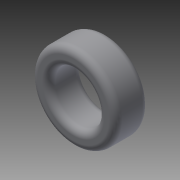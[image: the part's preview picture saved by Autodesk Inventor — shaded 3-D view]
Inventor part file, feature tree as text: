
AUTODESK INVENTOR PART (.ipt)
format: ipt  version: 2015 (Build 190159000, 159)  size: 142,336 bytes
history: native  units: mm
features: fillet x2, extrude x1, sketch x1
ambient origin geometry x8: Origin, YZ Plane, XZ Plane, XY Plane, X Axis, Y Axis, Z Axis, Center Point
bodies: Solid1 (feature_tree)
feature tree (4):
  extrude  "Extrusion1"  Depth=2.0mm
  fillet  "Fillet1"  Radius=2.0mm
  fillet  "Fillet2"  [1 undecoded]
  sketch  "Sketch1"  dims[d0=10.0mm d1=0.0mm d2=2.0mm d3=2.0mm]
note: 1 required parameter value undecoded (feature->parameter linkage not recoverable at this tier; creation-order binding heuristic only, values carry confidence <= 0.55)
